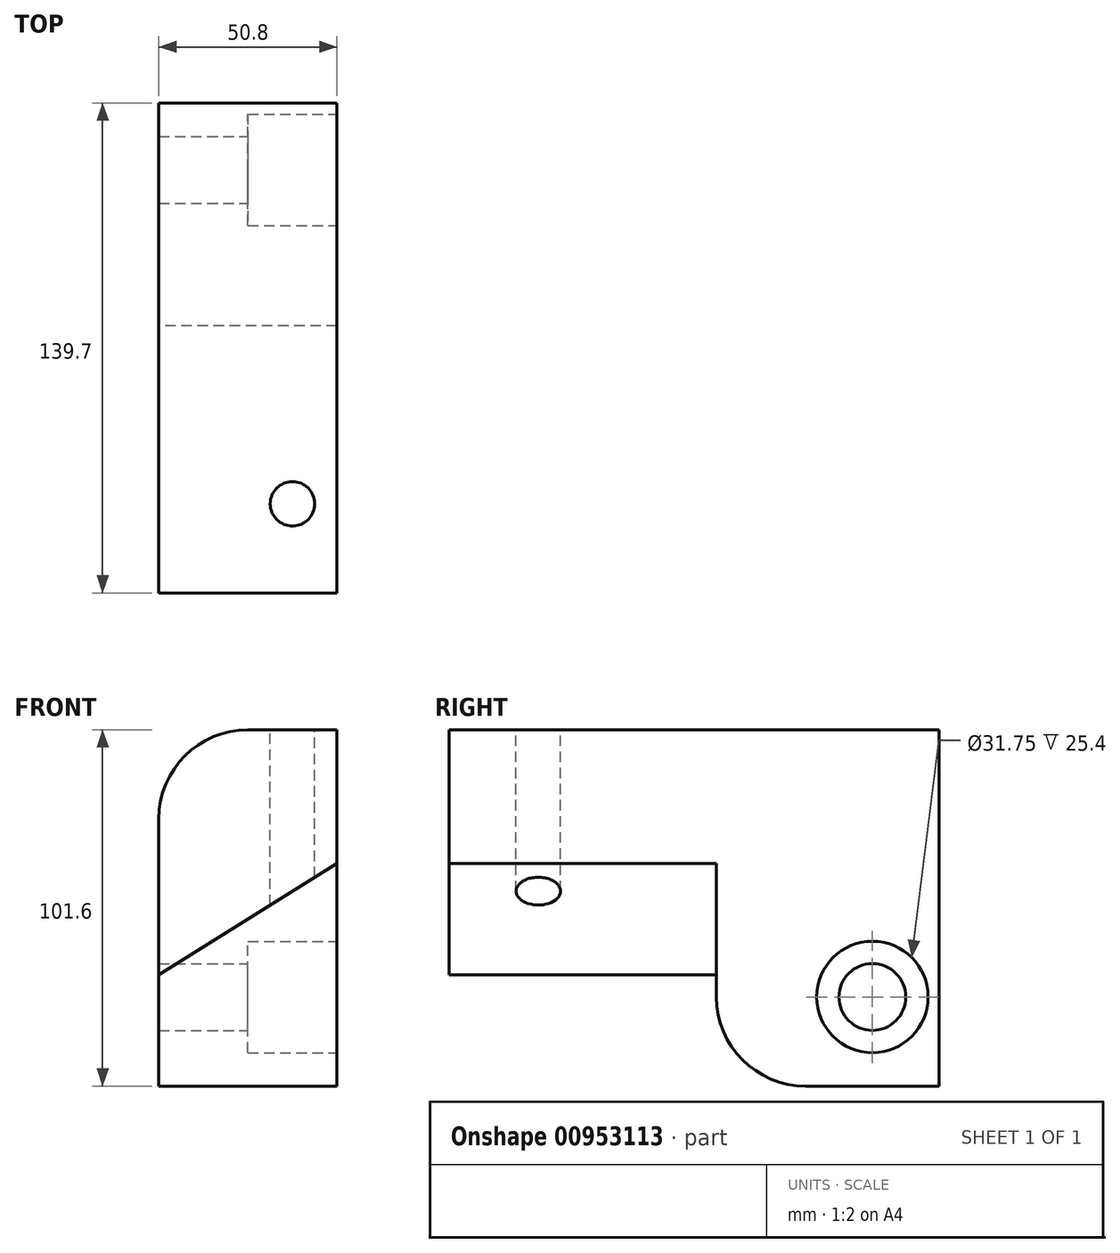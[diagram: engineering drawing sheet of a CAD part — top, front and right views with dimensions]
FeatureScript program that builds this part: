
annotation { "Feature Type Name" : "Feature", "Feature Type Description" : "" }
export const myFeature = defineFeature(function(context is Context, id is Id, definition is map)
    precondition{}
    {
        {
            var Q0;
            Q0=qCreatedBy(makeId("Front.planeOp"),FACE);
            var sketch = newSketch(context, id + "F0", { "sketchPlane" : qUnion([Q0])});
            skLineSegment(sketch, "E0", {"start": v(0, 0) * mm, "end": v(0, 44.45) * mm});
            skLineSegment(sketch, "E1", {"start": v(25.4, 69.85) * mm, "end": v(50.8, 69.85) * mm});
            skLineSegment(sketch, "E2", {"start": v(50.8, 69.85) * mm, "end": v(50.8, 31.75) * mm});
            skLineSegment(sketch, "E3", {"start": v(50.8, 31.75) * mm, "end": v(0, 0) * mm});
            skPoint(sketch, "E4.visualSharp", {"position": v(0, 69.85) * mm});
            skArc(sketch, "E4.filletArc", {"start": v(25.4, 69.85) * mm, "mid": v(7.44, 62.41) * mm, "end": v(0, 44.45) * mm});
            skLineSegment(sketch, "E5", {"start": v(50.8, 31.75) * mm, "end": v(50.8, -31.75) * mm});
            skLineSegment(sketch, "E6", {"start": v(50.8, -31.75) * mm, "end": v(0, -31.75) * mm});
            skLineSegment(sketch, "E7", {"start": v(0, -31.75) * mm, "end": v(0, 0) * mm});
            skSolve(sketch);
        }
        {
            var Q0;
            Q0=makeQuery(id+"F0.imprint","IMPRINT",FACE,{"disambiguationData":[TD([[makeQuery(id+"F0.imprint","IMPRINT",EDGE,{"derivedFrom":sQuery(id+"F0.wireOp",EDGE,"E0")}),-1.0]])]});
            extrude(context, id + "F1", {"entities" : qUnion([Q0]), "depth" : 139.7 * mm, "offsetDistance" : 25.4 * mm});
        }
        {
            var Q0;
            Q0=makeQuery(id+"F0.imprint","IMPRINT",FACE,{"disambiguationData":[TD([[makeQuery(id+"F0.imprint","IMPRINT",EDGE,{"derivedFrom":sQuery(id+"F0.wireOp",EDGE,"E3")}),1.0]])]});
            extrude(context, id + "F2", {"entities" : qUnion([Q0]), "operationType" : NewBodyOperationType.ADD, "depth" : 63.5 * mm, "offsetDistance" : 25.4 * mm});
        }
        {
            var Q0;
            Q0=makeQuery(id+"F2.opExtrude","CAP_EDGE",EDGE,{"disambiguationData":[OSD([sQuery(id+"F0.wireOp",EDGE,"E6")])],"isStart":false});
            fillet(context, id + "F3", {"entities" : qUnion([Q0]), "radius" : 25.4 * mm, "tangentPropagation" : true, "allowEdgeOverflow" : false});
        }
        {
            var Q0;
            Q0=makeQuery(id+"F2.boolean.opBoolean","MERGE",FACE,{"derivedFrom":[makeQuery(id+"F1.opExtrude","SWEPT_FACE",FACE,{"disambiguationData":[OSD([sQuery(id+"F0.wireOp",EDGE,"E2")])]}),makeQuery(id+"F2.opExtrude","SWEPT_FACE",FACE,{"disambiguationData":[OSD([sQuery(id+"F0.wireOp",EDGE,"E5")])]})]});
            var sketch = newSketch(context, id + "F4", { "sketchPlane" : qUnion([Q0])});
            skPoint(sketch, "E8", {"position": v(-19.05, -6.35) * mm});
            skSolve(sketch);
        }
        {
            var Q0;
            Q0=sQuery(id+"F4.wireOp",VERTEX,"E8");
            var Q1;
            Q1=makeQuery(id+"F1.opExtrude","SWEPT_BODY",BODY,{"disambiguationData":[OSD([sQuery(id+"F0.wireOp",EDGE,"E0"),sQuery(id+"F0.wireOp",EDGE,"E1"),sQuery(id+"F0.wireOp",EDGE,"E2"),sQuery(id+"F0.wireOp",EDGE,"E3"),sQuery(id+"F0.wireOp",EDGE,"E4.filletArc")])]});
            hole(context, id + "F5", {"style" : HoleStyle.C_BORE, "endStyle" : HoleEndStyle.THROUGH, "holeDiameter" : 19.05 * mm, "cBoreDiameter" : 31.75 * mm, "cBoreDepth" : 25.4 * mm, "majorDiameter" : 6.35 * mm, "isTappedThrough" : true, "tappedDepth" : 12.7 * mm, "tapClearance" : 3, "locations" : qUnion([Q0]), "scope" : qUnion([Q1])});
        }
        {
            var Q0;
            Q0=makeQuery(id+"F1.opExtrude","SWEPT_FACE",FACE,{"disambiguationData":[OSD([sQuery(id+"F0.wireOp",EDGE,"E1")])]});
            var sketch = newSketch(context, id + "F6", { "sketchPlane" : qUnion([Q0])});
            skPoint(sketch, "E9", {"position": v(38.1, -114.3) * mm});
            skSolve(sketch);
        }
        {
            var Q0;
            Q0=sQuery(id+"F6.wireOp",VERTEX,"E9");
            var Q1;
            Q1=makeQuery(id+"F1.opExtrude","SWEPT_BODY",BODY,{"disambiguationData":[OSD([sQuery(id+"F0.wireOp",EDGE,"E0"),sQuery(id+"F0.wireOp",EDGE,"E1"),sQuery(id+"F0.wireOp",EDGE,"E2"),sQuery(id+"F0.wireOp",EDGE,"E3"),sQuery(id+"F0.wireOp",EDGE,"E4.filletArc")])]});
            hole(context, id + "F7", {"style" : HoleStyle.SIMPLE, "endStyle" : HoleEndStyle.THROUGH, "holeDiameter" : 12.7 * mm, "majorDiameter" : 6.35 * mm, "isTappedThrough" : true, "tappedDepth" : 12.7 * mm, "tapClearance" : 3, "locations" : qUnion([Q0]), "scope" : qUnion([Q1])});
        }
    });
